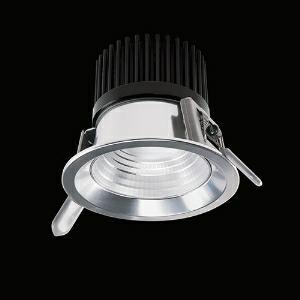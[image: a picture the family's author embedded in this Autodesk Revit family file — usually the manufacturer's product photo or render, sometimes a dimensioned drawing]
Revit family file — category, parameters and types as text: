
# Revit family: spectral_myral_myral_1500-840-s-dali
name_source: partatom
category: Lighting Fixtures
revit_build: Autodesk Revit 2016 (Build: 20150220_1215(x64)
units: mm (PartAtom-declared; Revit-internal decimal feet)

## family parameters
Cut with Voids When Loaded = No
Host = Face
Light Source = No
Part Type = Normal
Room Calculation Point = No
Round Connector Dimension = Use Diameter
Shared = No

## types (1)
- SPECTRAL MYRAL (1 x )
    Apparent Load = 0 VA
    Approval mark = CE
    CIE Flux Codes = 85 100 100 100 100
    Control Gear = Electronic transformer
    Default Elevation = 1800 mm
    Description = SPG0320173
MYRAL recessed spot

Design:
    Height = 0 mm  [stored 0 ft]
    Lamp = 1 x
    Lamp count = 1
    Length = 120 mm
    Luminous efficacy = 0 lm/W
    Manufacturer = Ridi
    ModVariant = No
    Model = MYRAL 1500-840-S-DALI
    Mounting Place = Ceiling
    Mounting Type = Recessed
    Number of Poles = 1
    OnlyDefault = Yes
    Power Factor = 1
    Product Name = SPECTRAL MYRAL
    Product group = Downlight recessed
    ProductGroupID = 400
    Protection Class = Protection class
    Protection Degree = IP 20
    RlxData = <blob elided: 38913 chars, md5=df19a359>
    Socket = socket
    Standby Power = 0 W
    System Light Flux = 0 lm
    System Power = 0 W
    Type Image = myral_04.jpg
    URL = http://reluxnet.relux.com
    VarID = ---
    Voltage = 0 V
    Weight = 0.00 kg
    Width = 0 mm  [stored 0 ft]

note: [stored X ft] marks values corroborated as IEEE doubles in the binary element streams (Revit-internal decimal feet)

## geometry (parser evidence)
native form markers: Sweep x10
no freeform markers — native parametric forms only
